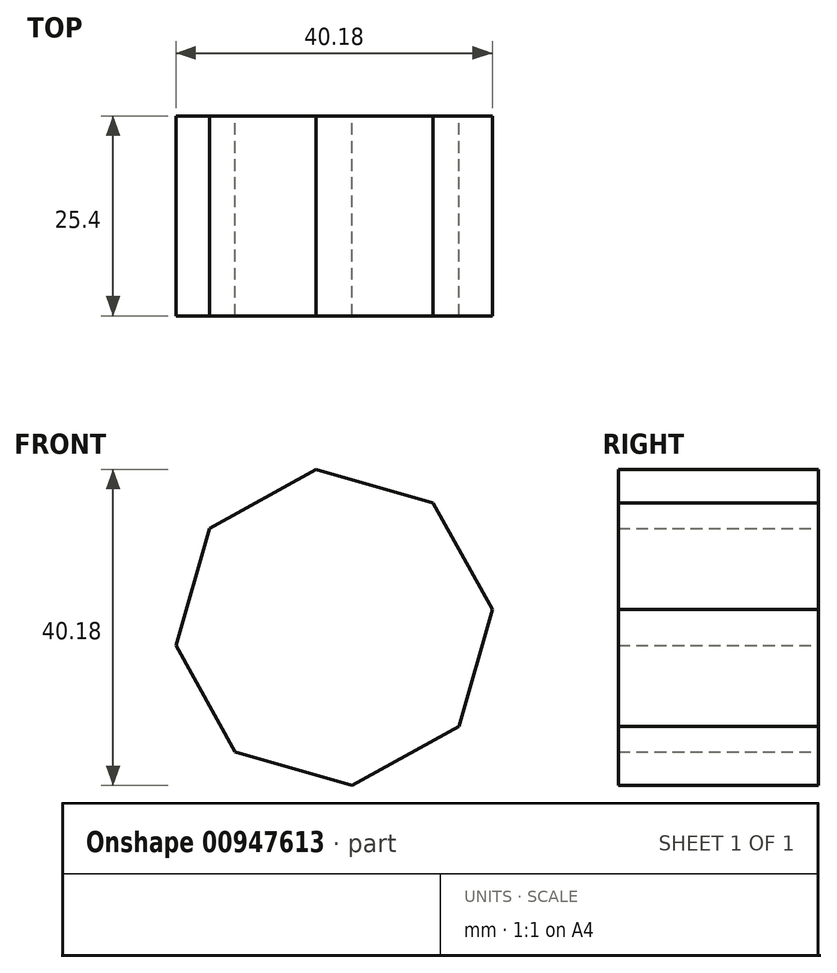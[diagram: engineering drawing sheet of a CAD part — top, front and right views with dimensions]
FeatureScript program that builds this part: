
annotation { "Feature Type Name" : "Feature", "Feature Type Description" : "" }
export const myFeature = defineFeature(function(context is Context, id is Id, definition is map)
    precondition{}
    {
        {
            var Q0;
            Q0=qCreatedBy(makeId("Front.planeOp"),FACE);
            var sketch = newSketch(context, id + "F0", { "sketchPlane" : qUnion([Q0])});
            skCircle(sketch, "E0.cCircle", {"center": v(-1.39, 0) * mm, "radius": 18.68 * mm, "construction": true});
            skLineSegment(sketch, "E0.0", {"start": v(18.7, 2.3) * mm, "end": v(14.44, -12.58) * mm});
            skLineSegment(sketch, "E0.1", {"start": v(14.44, -12.58) * mm, "end": v(0.9, -20.1) * mm});
            skLineSegment(sketch, "E0.2", {"start": v(0.9, -20.1) * mm, "end": v(-13.97, -15.83) * mm});
            skLineSegment(sketch, "E0.3", {"start": v(-13.97, -15.83) * mm, "end": v(-21.48, -2.3) * mm});
            skLineSegment(sketch, "E0.4", {"start": v(-21.48, -2.3) * mm, "end": v(-17.22, 12.58) * mm});
            skLineSegment(sketch, "E0.5", {"start": v(-17.22, 12.58) * mm, "end": v(-3.68, 20.1) * mm});
            skLineSegment(sketch, "E0.6", {"start": v(-3.68, 20.1) * mm, "end": v(11.2, 15.83) * mm});
            skLineSegment(sketch, "E0.7", {"start": v(11.2, 15.83) * mm, "end": v(18.7, 2.3) * mm});
            skPoint(sketch, "E0.0.midPoint", {"position": v(16.57, -5.14) * mm});
            skSolve(sketch);
        }
        {
            var Q0;
            Q0 = qSketchRegion(id + "F0", true);
            extrude(context, id + "F1", {"entities" : qUnion([Q0]), "depth" : 25.4 * mm, "offsetDistance" : 25.4 * mm});
        }
    });
